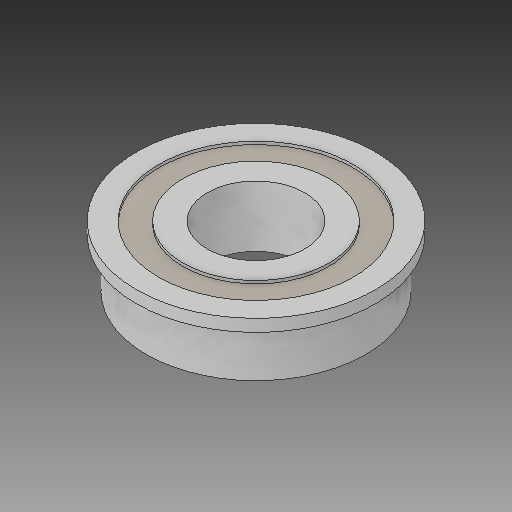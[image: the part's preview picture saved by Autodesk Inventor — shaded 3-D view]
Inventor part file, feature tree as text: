
AUTODESK INVENTOR PART (.ipt)
format: ipt  version: 2017 (Build 210142000, 142)  size: 144,384 bytes
history: native  units: in
note: dims shown in document units (in); Inventor stores cm internally (conversion verified against a paired STEP export)
features: revolve x1
ambient origin geometry x8: Origin, YZ Plane, XZ Plane, XY Plane, X Axis, Y Axis, Z Axis, Center Point
bodies: Solid1 (feature_tree)
feature tree (1):
  revolve  "Revolve1"  [1 undecoded]
note: 1 required parameter value undecoded (feature->parameter linkage not recoverable at this tier; creation-order binding heuristic only, values carry confidence <= 0.55)
